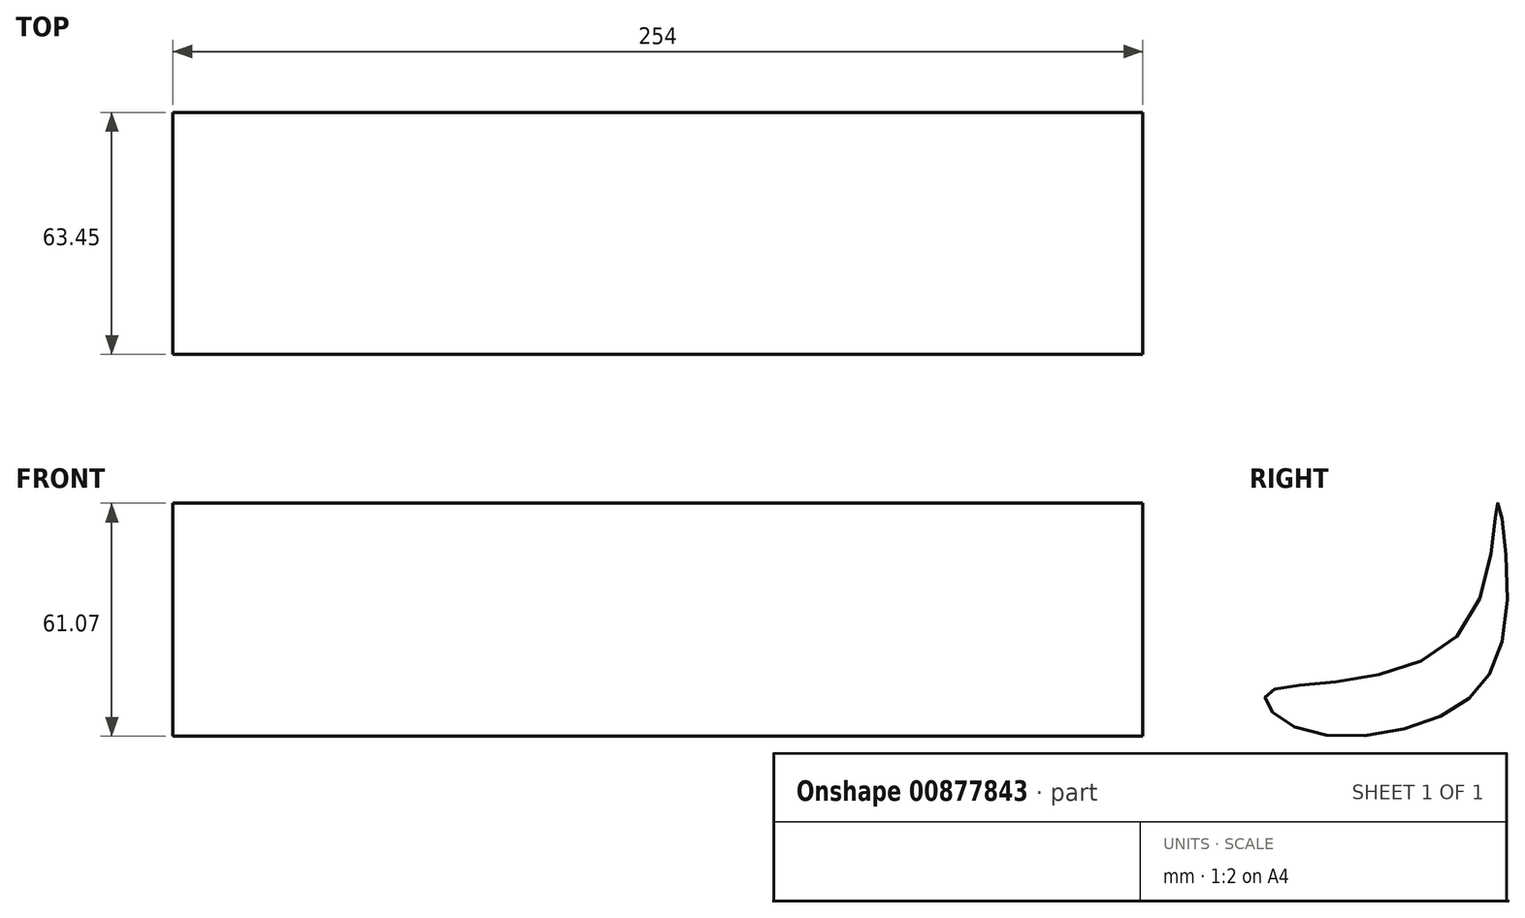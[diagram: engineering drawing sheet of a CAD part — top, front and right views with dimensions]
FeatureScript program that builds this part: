
annotation { "Feature Type Name" : "Feature", "Feature Type Description" : "" }
export const myFeature = defineFeature(function(context is Context, id is Id, definition is map)
    precondition{}
    {
        {
            var Q0;
            Q0=qCreatedBy(makeId("Right.planeOp"),FACE);
            var sketch = newSketch(context, id + "F0", { "sketchPlane" : qUnion([Q0])});
            skFitSpline(sketch, "E0", {"points": [v(0, -28.6) * mm, v(43.58, -13.08) * mm, v(51.97, 19.07) * mm, v(54.07, -12.27) * mm, v(37.28, -36.59) * mm, v(0, -40.07) * mm, v(-8.88, -31.68) * mm, v(0, -28.6) * mm]});
            skSolve(sketch);
        }
        {
            var Q0;
            Q0=makeQuery(id+"F0.imprint","IMPRINT",FACE,{"disambiguationData":[TD([[makeQuery(id+"F0.imprint","IMPRINT",EDGE,{"derivedFrom":sQuery(id+"F0.wireOp",EDGE,"E0")}),-1.0]])]});
            extrude(context, id + "F1", {"entities" : qUnion([Q0]), "oppositeDirection" : true, "depth" : 254 * mm, "offsetDistance" : 25.4 * mm});
        }
    });
